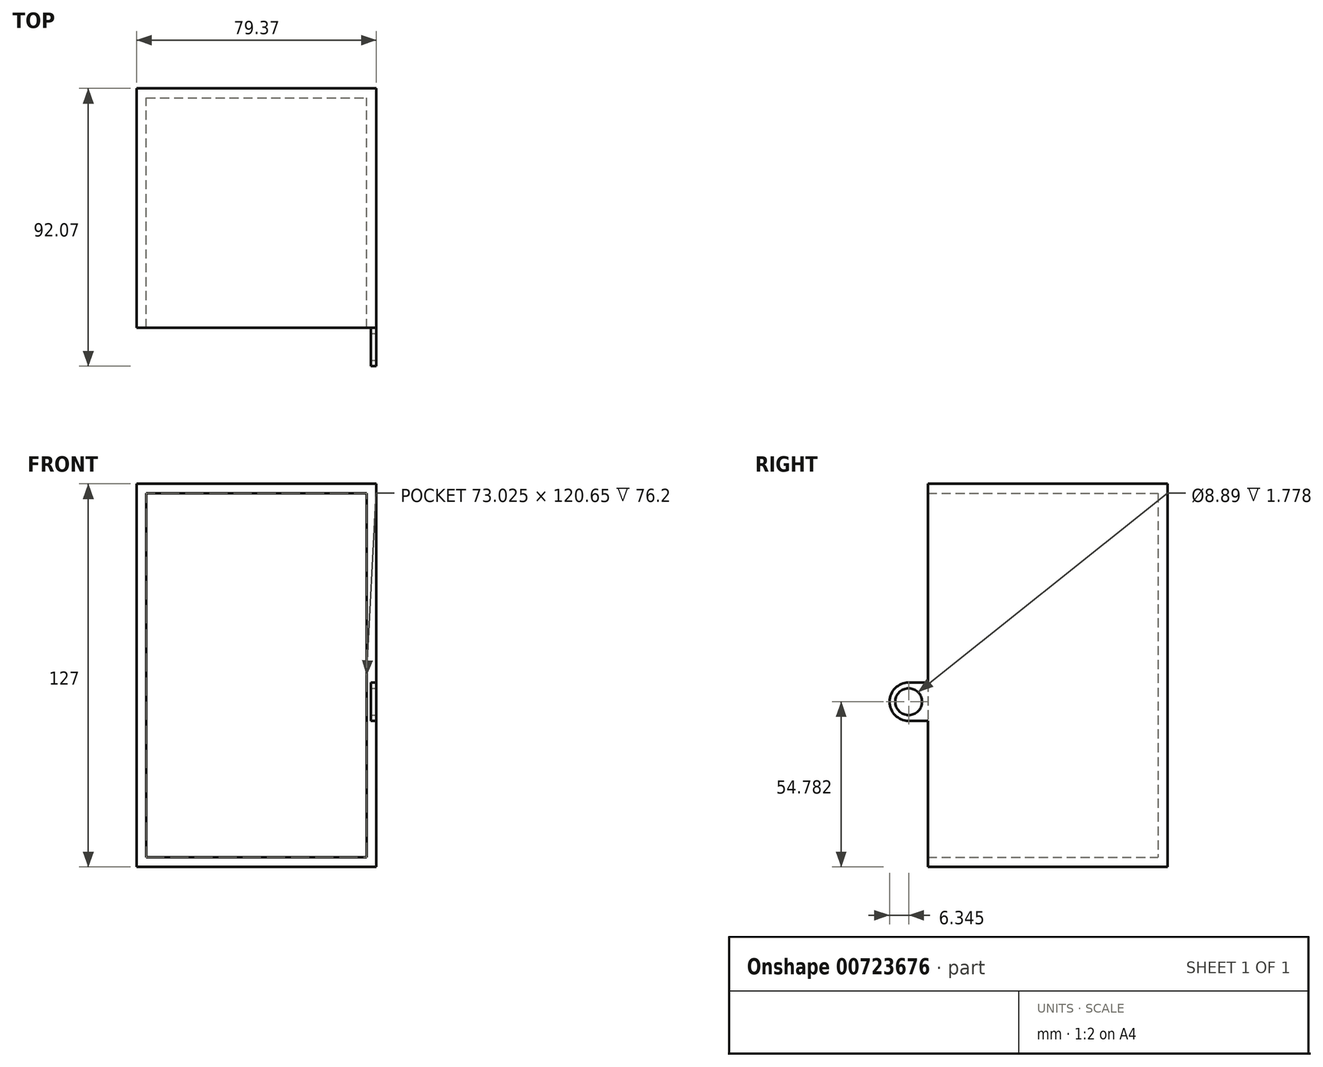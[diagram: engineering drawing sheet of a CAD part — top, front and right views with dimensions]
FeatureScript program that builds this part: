
annotation { "Feature Type Name" : "Feature", "Feature Type Description" : "" }
export const myFeature = defineFeature(function(context is Context, id is Id, definition is map)
    precondition{}
    {
        {
            var Q0;
            Q0=qCreatedBy(makeId("Front.planeOp"),FACE);
            var sketch = newSketch(context, id + "F0", { "sketchPlane" : qUnion([Q0])});
            skLineSegment(sketch, "E0.bottom", {"start": v(-49.86, 66.7) * mm, "end": v(29.51, 66.7) * mm});
            skLineSegment(sketch, "E0.top", {"start": v(-49.86, -60.3) * mm, "end": v(29.51, -60.3) * mm});
            skLineSegment(sketch, "E0.left", {"start": v(-49.86, 66.7) * mm, "end": v(-49.86, -60.3) * mm});
            skLineSegment(sketch, "E0.right", {"start": v(29.51, 66.7) * mm, "end": v(29.51, -60.3) * mm});
            skSolve(sketch);
        }
        {
            var Q0;
            Q0=makeQuery(id+"F0.imprint","IMPRINT",FACE,{"disambiguationData":[TD([[makeQuery(id+"F0.imprint","IMPRINT",EDGE,{"derivedFrom":sQuery(id+"F0.wireOp",EDGE,"E0.bottom")}),-1.0]])]});
            extrude(context, id + "F1", {"entities" : qUnion([Q0]), "depth" : 3.17 * mm, "offsetDistance" : 25.4 * mm});
        }
        {
            var Q0;
            Q0=makeQuery(id+"F1.opExtrude","CAP_FACE",FACE,{"disambiguationData":[OSD([sQuery(id+"F0.wireOp",EDGE,"E0.bottom"),sQuery(id+"F0.wireOp",EDGE,"E0.top"),sQuery(id+"F0.wireOp",EDGE,"E0.left"),sQuery(id+"F0.wireOp",EDGE,"E0.right")])],"isStart":false});
            var sketch = newSketch(context, id + "F2", { "sketchPlane" : qUnion([Q0])});
            skLineSegment(sketch, "E1.bottom", {"start": v(-46.69, 66.7) * mm, "end": v(-49.86, 66.7) * mm});
            skLineSegment(sketch, "E1.top", {"start": v(-46.69, -60.3) * mm, "end": v(-49.86, -60.3) * mm});
            skLineSegment(sketch, "E1.left", {"start": v(-46.69, 66.7) * mm, "end": v(-46.69, -60.3) * mm});
            skLineSegment(sketch, "E1.right", {"start": v(-49.86, 66.7) * mm, "end": v(-49.86, -60.3) * mm});
            skLineSegment(sketch, "E2.bottom", {"start": v(26.34, 66.7) * mm, "end": v(29.51, 66.7) * mm});
            skLineSegment(sketch, "E2.top", {"start": v(26.34, -60.3) * mm, "end": v(29.51, -60.3) * mm});
            skLineSegment(sketch, "E2.left", {"start": v(26.34, 66.7) * mm, "end": v(26.34, -60.3) * mm});
            skLineSegment(sketch, "E2.right", {"start": v(29.51, 66.7) * mm, "end": v(29.51, -60.3) * mm});
            skLineSegment(sketch, "E3.bottom", {"start": v(-46.69, 63.53) * mm, "end": v(26.34, 63.53) * mm});
            skLineSegment(sketch, "E3.top", {"start": v(-46.69, 66.7) * mm, "end": v(26.34, 66.7) * mm});
            skLineSegment(sketch, "E3.left", {"start": v(-46.69, 63.53) * mm, "end": v(-46.69, 66.7) * mm});
            skLineSegment(sketch, "E3.right", {"start": v(26.34, 63.53) * mm, "end": v(26.34, 66.7) * mm});
            skLineSegment(sketch, "E4.bottom", {"start": v(-46.69, -57.12) * mm, "end": v(26.34, -57.12) * mm});
            skLineSegment(sketch, "E4.top", {"start": v(-46.69, -60.3) * mm, "end": v(26.34, -60.3) * mm});
            skLineSegment(sketch, "E4.left", {"start": v(-46.69, -57.12) * mm, "end": v(-46.69, -60.3) * mm});
            skLineSegment(sketch, "E4.right", {"start": v(26.34, -57.12) * mm, "end": v(26.34, -60.3) * mm});
            skSolve(sketch);
        }
        {
            var Q0;
            Q0=makeQuery(id+"F2.imprint","IMPRINT",FACE,{"disambiguationData":[TD([[makeQuery(id+"F2.imprint","IMPRINT",EDGE,{"derivedFrom":sQuery(id+"F2.wireOp",EDGE,"E1.bottom")}),-1.0]])]});
            var Q1;
            Q1=makeQuery(id+"F2.imprint","IMPRINT",FACE,{"disambiguationData":[TD([[makeQuery(id+"F2.imprint","IMPRINT",EDGE,{"derivedFrom":sQuery(id+"F2.wireOp",EDGE,"E3.bottom")}),1.0]])]});
            var Q2;
            Q2=makeQuery(id+"F2.imprint","IMPRINT",FACE,{"disambiguationData":[TD([[makeQuery(id+"F2.imprint","IMPRINT",EDGE,{"derivedFrom":sQuery(id+"F2.wireOp",EDGE,"E2.bottom")}),-1.0]])]});
            var Q3;
            Q3=makeQuery(id+"F2.imprint","IMPRINT",FACE,{"disambiguationData":[TD([[makeQuery(id+"F2.imprint","IMPRINT",EDGE,{"derivedFrom":sQuery(id+"F2.wireOp",EDGE,"E4.bottom")}),-1.0]])]});
            extrude(context, id + "F3", {"entities" : qUnion([Q0, Q1, Q2, Q3]), "operationType" : NewBodyOperationType.ADD, "depth" : 76.2 * mm, "offsetDistance" : 25.4 * mm});
        }
        {
            var Q0;
            Q0=makeQuery(id+"F3.opExtrude","CAP_FACE",FACE,{"disambiguationData":[OSD([sQuery(id+"F2.wireOp",EDGE,"E1.bottom"),sQuery(id+"F2.wireOp",EDGE,"E1.top"),sQuery(id+"F2.wireOp",EDGE,"E1.left"),sQuery(id+"F2.wireOp",EDGE,"E1.right"),sQuery(id+"F2.wireOp",EDGE,"E2.bottom"),sQuery(id+"F2.wireOp",EDGE,"E2.top"),sQuery(id+"F2.wireOp",EDGE,"E2.left"),sQuery(id+"F2.wireOp",EDGE,"E2.right"),sQuery(id+"F2.wireOp",EDGE,"E3.bottom"),sQuery(id+"F2.wireOp",EDGE,"E3.top"),sQuery(id+"F2.wireOp",EDGE,"E4.bottom"),sQuery(id+"F2.wireOp",EDGE,"E4.top")])],"isStart":false});
            var sketch = newSketch(context, id + "F4", { "sketchPlane" : qUnion([Q0])});
            skLineSegment(sketch, "E5.bottom", {"start": v(27.74, 0.84) * mm, "end": v(29.51, 0.84) * mm});
            skLineSegment(sketch, "E5.top", {"start": v(27.74, -11.86) * mm, "end": v(29.51, -11.86) * mm});
            skLineSegment(sketch, "E5.left", {"start": v(27.74, 0.84) * mm, "end": v(27.74, -11.86) * mm});
            skLineSegment(sketch, "E5.right", {"start": v(29.51, 0.84) * mm, "end": v(29.51, -11.86) * mm});
            skSolve(sketch);
        }
        {
            var Q0;
            Q0=makeQuery(id+"F4.imprint","IMPRINT",FACE,{"disambiguationData":[TD([[makeQuery(id+"F4.imprint","IMPRINT",EDGE,{"derivedFrom":sQuery(id+"F4.wireOp",EDGE,"E5.bottom")}),-1.0]])]});
            extrude(context, id + "F5", {"entities" : qUnion([Q0]), "operationType" : NewBodyOperationType.ADD, "depth" : 12.7 * mm, "offsetDistance" : 25.4 * mm});
        }
        {
            var Q0;
            Q0=makeQuery(id+"F5.opExtrude","CAP_EDGE",EDGE,{"disambiguationData":[OSD([sQuery(id+"F4.wireOp",EDGE,"E5.bottom")])],"isStart":false});
            fillet(context, id + "F6", {"entities" : qUnion([Q0]), "radius" : 6.35 * mm, "tangentPropagation" : true, "allowEdgeOverflow" : false});
        }
        {
            var Q0;
            Q0=makeQuery(id+"F5.opExtrude","CAP_EDGE",EDGE,{"disambiguationData":[OSD([sQuery(id+"F4.wireOp",EDGE,"E5.top")])],"isStart":false});
            fillet(context, id + "F7", {"entities" : qUnion([Q0]), "radius" : 6.35 * mm, "tangentPropagation" : true, "allowEdgeOverflow" : false});
        }
        {
            var Q0;
            Q0=makeQuery(id+"F5.boolean.opBoolean","MERGE",FACE,{"derivedFrom":[makeQuery(id+"F3.boolean.opBoolean","MERGE",FACE,{"derivedFrom":[makeQuery(id+"F1.opExtrude","SWEPT_FACE",FACE,{"disambiguationData":[OSD([sQuery(id+"F0.wireOp",EDGE,"E0.right")])]}),makeQuery(id+"F3.opExtrude","SWEPT_FACE",FACE,{"disambiguationData":[OSD([sQuery(id+"F2.wireOp",EDGE,"E2.right")])]})]}),makeQuery(id+"F5.opExtrude","SWEPT_FACE",FACE,{"disambiguationData":[OSD([sQuery(id+"F4.wireOp",EDGE,"E5.right")])]})]});
            var sketch = newSketch(context, id + "F8", { "sketchPlane" : qUnion([Q0])});
            skCircle(sketch, "E6", {"center": v(-85.73, -5.5) * mm, "radius": 4.45 * mm});
            skSolve(sketch);
        }
        {
            var Q0;
            Q0=makeQuery(id+"F8.imprint","IMPRINT",FACE,{"disambiguationData":[TD([[makeQuery(id+"F8.imprint","IMPRINT",EDGE,{"derivedFrom":sQuery(id+"F8.wireOp",EDGE,"E6")}),1.0]])]});
            extrude(context, id + "F9", {"entities" : qUnion([Q0]), "operationType" : NewBodyOperationType.REMOVE, "oppositeDirection" : true, "depth" : 25.4 * mm, "offsetDistance" : 25.4 * mm});
        }
    });
